# Revit family: ASL_64_Series_timber_door_mullion
name_source: partatom
category: Detail Items
revit_build: Autodesk Revit 2018 (Build: 20170223_1515(x64)
units: mm (PartAtom-declared; Revit-internal decimal feet)

## family parameters
Rotate with component = No
Section Shape = Not Defined
Shared = Yes

## types (5) — shared parameters
Door Mullion Post_ASL_544 = Yes
Glazing_2 = Yes
Manufacturer = Aluminate Solutions Limited

## per-type parameters (varying)
| type | 40mm Door Depth Parametric | 50mm Door Depth Parametric | Door Stop_40 | Door Stop_50 | Door_40 | Door_50 | Flush Infill | Glazing | Hinge Depth Parametric | Technical Info | Type Comments |
| Double Action Door 40mm | 19 mm  [stored 0.062336 ft] | 25 mm  [stored 0.082021 ft] | No | No | Yes | No | Yes | No | 48 mm  [stored 0.15748 ft] | www.aluminate.nz | ASL 64 Series Mullion With Double Action 40mm Timber Door |
| Double Action Door 50mm | 19 mm  [stored 0.062336 ft] | 25 mm  [stored 0.082021 ft] | No | No | No | Yes | Yes | No | 52 mm | ww.aluminate.nz | ASL 64 Series Mullion With Double Action 50mm Timber Door |
| Single Action Door 40mm | 48 mm  [stored 0.15748 ft] | 52 mm | Yes | No | Yes | No | No | No | 48 mm  [stored 0.15748 ft] | www.aluminate.nz | ASL 64 Series Mullion With Single Action 40mm Timber Door |
| Single Action Door 50mm | 48 mm  [stored 0.15748 ft] | 52 mm | No | Yes | No | Yes | No | No | 52 mm | www.aluminate.nz | ASL 64 Series Mullion With Single Action 50mm Timber Door |
| Glazing | 48 mm  [stored 0.15748 ft] | 52 mm | No | No | No | No | No | Yes | 51 mm  [stored 0.167323 ft] | www.aluminate.nz | ASL 64 Series Mullion With Glazing |

note: [stored X ft] marks values corroborated as IEEE doubles in the binary element streams (Revit-internal decimal feet)

## geometry (parser evidence)
native form markers: Sweep x7
no freeform markers — native parametric forms only
